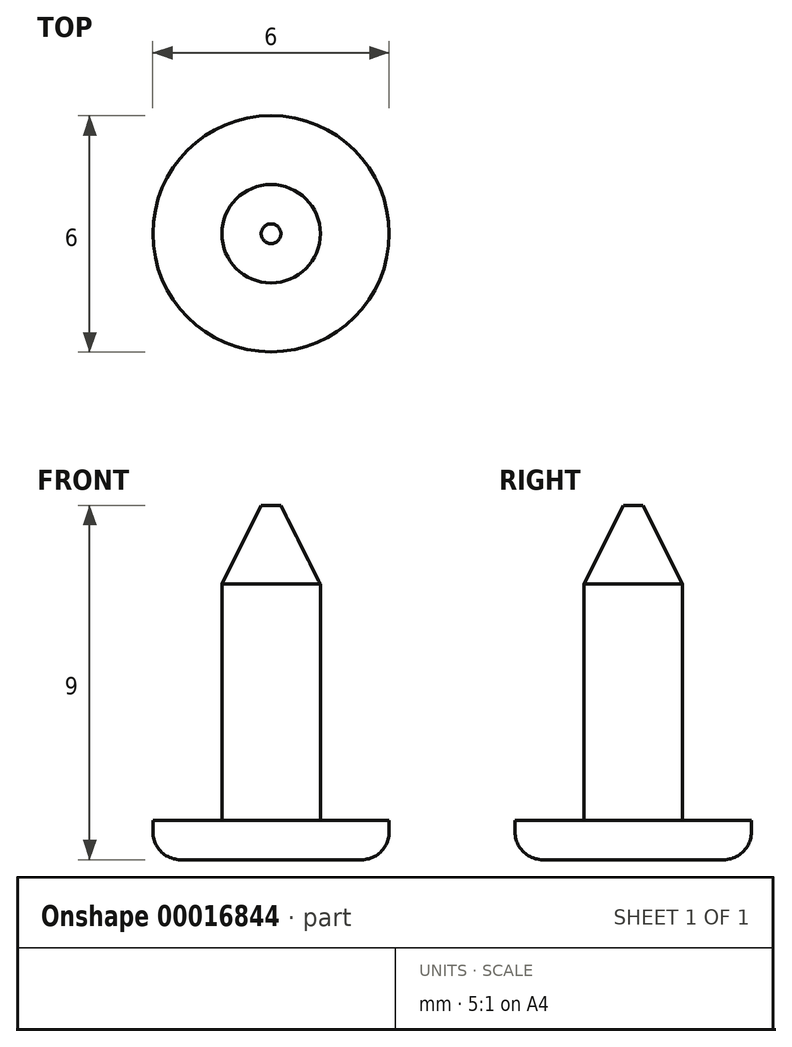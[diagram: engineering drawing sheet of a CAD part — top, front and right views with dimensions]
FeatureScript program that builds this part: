
annotation { "Feature Type Name" : "Feature", "Feature Type Description" : "" }
export const myFeature = defineFeature(function(context is Context, id is Id, definition is map)
    precondition{}
    {
        {
            var Q0;
            Q0=qCreatedBy(makeId("Top.planeOp"),FACE);
            var sketch = newSketch(context, id + "F0", { "sketchPlane" : qUnion([Q0])});
            skCircle(sketch, "E0", {"center": v(-115.13, -30.03) * mm, "radius": 3 * mm});
            skCircle(sketch, "E1", {"center": v(-115.13, -30.03) * mm, "radius": 1.25 * mm});
            skSolve(sketch);
        }
        {
            var Q0;
            Q0=makeQuery(id+"F0.imprint","IMPRINT",FACE,{"disambiguationData":[TD([[makeQuery(id+"F0.imprint","IMPRINT",EDGE,{"derivedFrom":sQuery(id+"F0.wireOp",EDGE,"E1")}),1.0]])]});
            extrude(context, id + "F1", {"entities" : qUnion([Q0]), "depth" : 9 * mm});
        }
        {
            var Q0;
            Q0=makeQuery(id+"F0.imprint","IMPRINT",FACE,{"disambiguationData":[TD([[makeQuery(id+"F0.imprint","IMPRINT",EDGE,{"derivedFrom":sQuery(id+"F0.wireOp",EDGE,"E0")}),1.0]])]});
            extrude(context, id + "F2", {"entities" : qUnion([Q0]), "operationType" : NewBodyOperationType.ADD, "depth" : 1 * mm});
        }
        {
            var Q0;
            Q0=makeQuery(id+"F1.opExtrude","CAP_EDGE",EDGE,{"disambiguationData":[OSD([sQuery(id+"F0.wireOp",EDGE,"E1")])],"isStart":false});
            chamfer(context, id + "F3", {"entities" : qUnion([Q0]), "chamferType" : ChamferType.TWO_OFFSETS, "width1" : 1 * mm, "oppositeDirection" : false, "width2" : 2 * mm, "tangentPropagation" : true});
        }
        {
            var Q0;
            Q0=makeQuery(id+"F2.opExtrude","CAP_EDGE",EDGE,{"disambiguationData":[OSD([sQuery(id+"F0.wireOp",EDGE,"E0")])],"isStart":true});
            fillet(context, id + "F4", {"entities" : qUnion([Q0]), "radius" : .7 * mm, "tangentPropagation" : true, "allowEdgeOverflow" : false});
        }
    });
